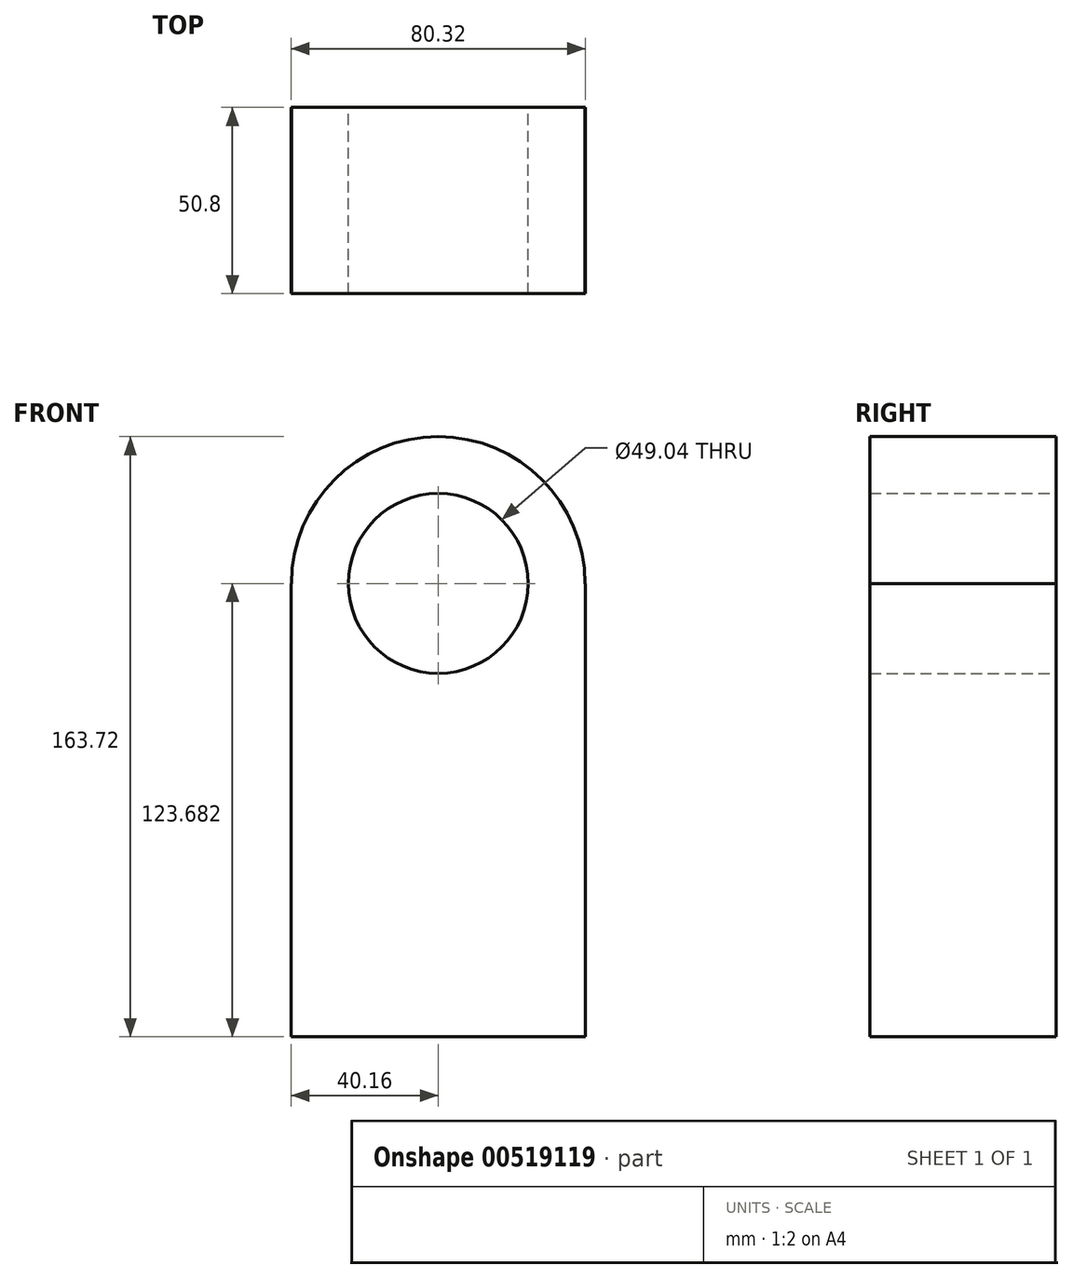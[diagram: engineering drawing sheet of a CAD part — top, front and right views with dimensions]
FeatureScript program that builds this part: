
annotation { "Feature Type Name" : "Feature", "Feature Type Description" : "" }
export const myFeature = defineFeature(function(context is Context, id is Id, definition is map)
    precondition{}
    {
        {
            var Q0;
            Q0=qCreatedBy(makeId("Front.planeOp"),FACE);
            var sketch = newSketch(context, id + "F0", { "sketchPlane" : qUnion([Q0])});
            skLineSegment(sketch, "E0.bottom", {"start": v(-40.16, 61.84) * mm, "end": v(-40.04, 61.84) * mm});
            skLineSegment(sketch, "E0.top", {"start": v(-40.16, -61.84) * mm, "end": v(40.16, -61.84) * mm});
            skLineSegment(sketch, "E0.left", {"start": v(-40.16, 61.84) * mm, "end": v(-40.16, -61.84) * mm});
            skLineSegment(sketch, "E0.right", {"start": v(40.16, 61.84) * mm, "end": v(40.16, -61.84) * mm});
            skPoint(sketch, "E0.middle", {"position": v(0, 0) * mm});
            skArc(sketch, "E1", {"start": v(40.04, 61.84) * mm, "mid": v(0, 101.88) * mm, "end": v(-40.04, 61.84) * mm});
            skCircle(sketch, "E2", {"center": v(0, 61.84) * mm, "radius": 24.52 * mm});
            skLineSegment(sketch, "E3.trimOffspring", {"start": v(40.04, 61.84) * mm, "end": v(40.16, 61.84) * mm});
            skSolve(sketch);
        }
        {
            var Q0;
            Q0=makeQuery(id+"F0.imprint","IMPRINT",FACE,{"disambiguationData":[TD([[makeQuery(id+"F0.imprint","IMPRINT",EDGE,{"derivedFrom":sQuery(id+"F0.wireOp",EDGE,"E0.bottom")}),-1.0]])]});
            extrude(context, id + "F1", {"entities" : qUnion([Q0]), "depth" : 50.8 * mm});
        }
    });
